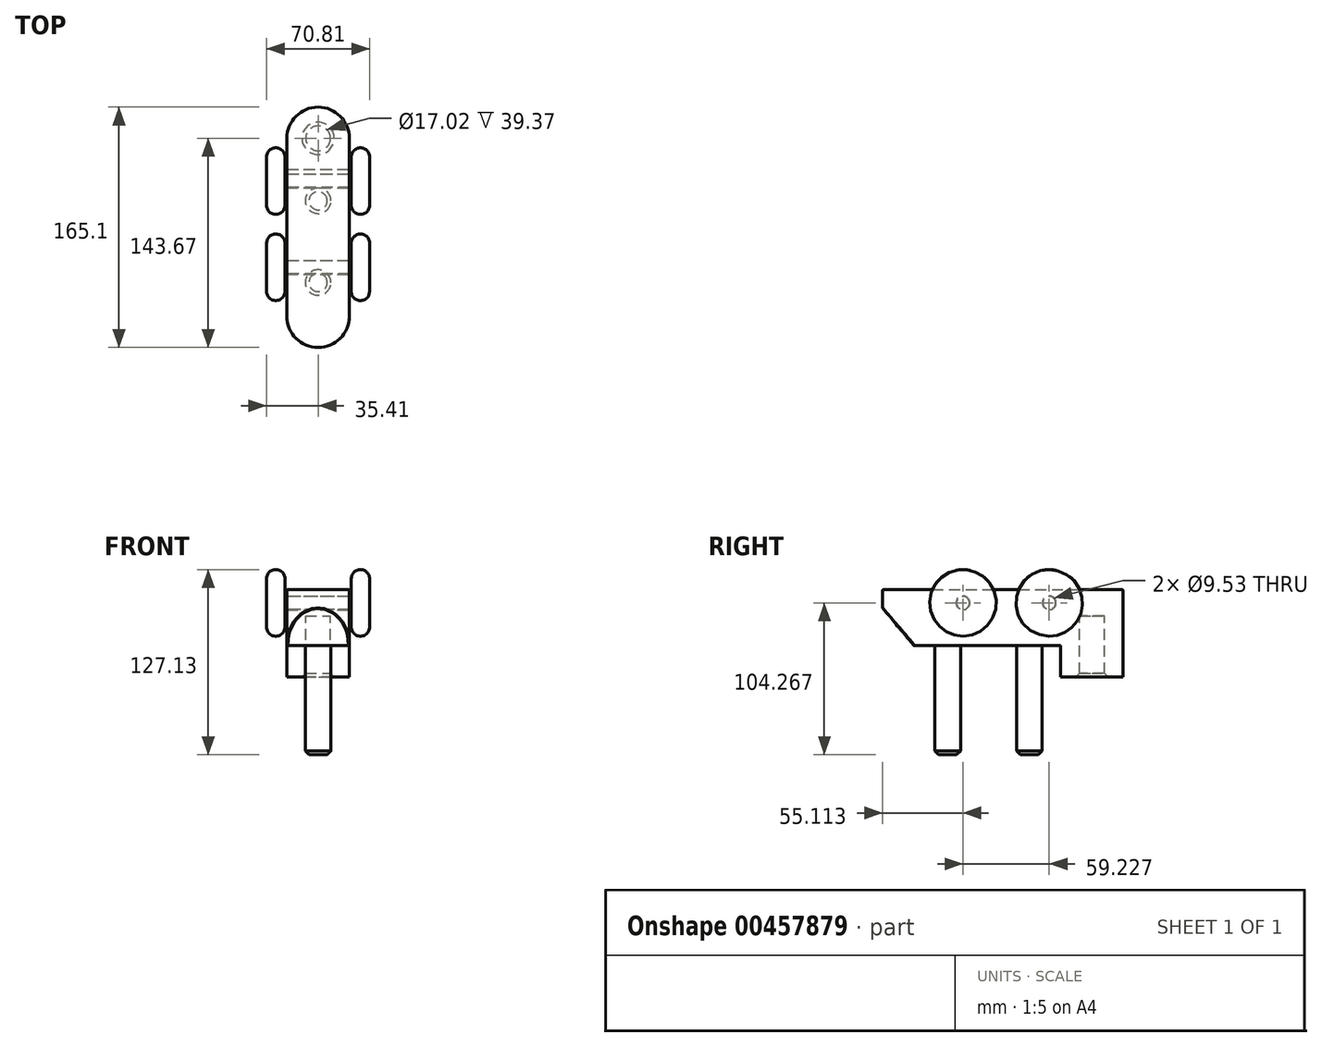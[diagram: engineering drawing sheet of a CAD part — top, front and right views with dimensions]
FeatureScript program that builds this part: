
annotation { "Feature Type Name" : "Feature", "Feature Type Description" : "" }
export const myFeature = defineFeature(function(context is Context, id is Id, definition is map)
    precondition{}
    {
        {
            var Q0;
            Q0=qCreatedBy(makeId("Top.planeOp"),FACE);
            var sketch = newSketch(context, id + "F0", { "sketchPlane" : qUnion([Q0])});
            skLineSegment(sketch, "E0", {"start": v(-21.43, 0) * mm, "end": v(-21.43, -122.24) * mm});
            skLineSegment(sketch, "E1", {"start": v(0, -143.67) * mm, "end": v(0, -143.67) * mm});
            skLineSegment(sketch, "E2", {"start": v(21.43, -122.24) * mm, "end": v(21.43, 0) * mm});
            skLineSegment(sketch, "E3", {"start": v(0, 21.43) * mm, "end": v(0, 21.43) * mm});
            skArc(sketch, "E4.filletArc", {"start": v(0, 21.43) * mm, "mid": v(-15.15, 15.15) * mm, "end": v(-21.43, 0) * mm});
            skArc(sketch, "E5.filletArc", {"start": v(21.43, 0) * mm, "mid": v(15.15, 15.15) * mm, "end": v(0, 21.43) * mm});
            skArc(sketch, "E6.filletArc", {"start": v(-21.43, -122.24) * mm, "mid": v(-15.15, -137.4) * mm, "end": v(0, -143.67) * mm});
            skArc(sketch, "E7.filletArc", {"start": v(0, -143.67) * mm, "mid": v(15.15, -137.4) * mm, "end": v(21.43, -122.24) * mm});
            skLineSegment(sketch, "E8", {"start": v(-21.43, -21.43) * mm, "end": v(21.43, -21.43) * mm});
            skCircle(sketch, "E9", {"center": v(0, 0) * mm, "radius": 8.5 * mm});
            skCircle(sketch, "E10", {"center": v(0, -99.03) * mm, "radius": 8.76 * mm});
            skCircle(sketch, "E11", {"center": v(0, -42.9) * mm, "radius": 8.76 * mm});
            skLineSegment(sketch, "E12", {"start": v(-21.43, -122.24) * mm, "end": v(21.43, -122.24) * mm, "construction": true});
            skSolve(sketch);
        }
        {
            var Q0;
            {var subQ3=sQuery(id+"F0.wireOp",EDGE,"E6.filletArc");Q0=makeQuery(id+"F0.imprint","IMPRINT",FACE,{"disambiguationData":[TD([[makeQuery(id+"F0.imprint","IMPRINT",EDGE,{"derivedFrom":subQ3}),1.0]])]});}
            var Q1;
            {var subQ0=sQuery(id+"F0.wireOp",EDGE,"E4.filletArc");Q1=makeQuery(id+"F0.imprint","IMPRINT",FACE,{"disambiguationData":[TD([[makeQuery(id+"F0.imprint","IMPRINT",EDGE,{"derivedFrom":subQ0}),1.0]])]});}
            var Q2;
            Q2=makeQuery(id+"F0.imprint","IMPRINT",FACE,{"disambiguationData":[TD([[makeQuery(id+"F0.imprint","IMPRINT",EDGE,{"derivedFrom":sQuery(id+"F0.wireOp",EDGE,"E11")}),1.0]])]});
            var Q3;
            Q3=makeQuery(id+"F0.imprint","IMPRINT",FACE,{"disambiguationData":[TD([[makeQuery(id+"F0.imprint","IMPRINT",EDGE,{"derivedFrom":sQuery(id+"F0.wireOp",EDGE,"E10")}),1.0]])]});
            var Q4;
            Q4=makeQuery(id+"F0.imprint","IMPRINT",FACE,{"disambiguationData":[TD([[makeQuery(id+"F0.imprint","IMPRINT",EDGE,{"derivedFrom":sQuery(id+"F0.wireOp",EDGE,"E9")}),1.0]])]});
            extrude(context, id + "F1", {"entities" : qUnion([Q0, Q1, Q2, Q3, Q4]), "depth" : 38.35 * mm, "offsetDistance" : 25.4 * mm});
        }
        {
            var Q0;
            {var subQ0=sQuery(id+"F0.wireOp",EDGE,"E4.filletArc");Q0=makeQuery(id+"F0.imprint","IMPRINT",FACE,{"disambiguationData":[TD([[makeQuery(id+"F0.imprint","IMPRINT",EDGE,{"derivedFrom":subQ0}),1.0]])]});}
            var Q1;
            Q1=makeQuery(id+"F0.imprint","IMPRINT",FACE,{"disambiguationData":[TD([[makeQuery(id+"F0.imprint","IMPRINT",EDGE,{"derivedFrom":sQuery(id+"F0.wireOp",EDGE,"E9")}),1.0]])]});
            extrude(context, id + "F2", {"entities" : qUnion([Q0, Q1]), "operationType" : NewBodyOperationType.REMOVE, "depth" : 20.32 * mm, "offsetDistance" : 25.4 * mm});
        }
        {
            var Q0;
            Q0=makeQuery(id+"F0.imprint","IMPRINT",FACE,{"disambiguationData":[TD([[makeQuery(id+"F0.imprint","IMPRINT",EDGE,{"derivedFrom":sQuery(id+"F0.wireOp",EDGE,"E11")}),1.0]])]});
            var Q1;
            Q1=makeQuery(id+"F0.imprint","IMPRINT",FACE,{"disambiguationData":[TD([[makeQuery(id+"F0.imprint","IMPRINT",EDGE,{"derivedFrom":sQuery(id+"F0.wireOp",EDGE,"E10")}),1.0]])]});
            extrude(context, id + "F3", {"entities" : qUnion([Q0, Q1]), "operationType" : NewBodyOperationType.ADD, "oppositeDirection" : true, "depth" : 74.93 * mm, "offsetDistance" : 25.4 * mm});
        }
        {
            var Q0;
            Q0=makeQuery(id+"F2.boolean.opBoolean","COPY",FACE,{"derivedFrom":makeQuery(id+"F2.opExtrude","CAP_FACE",FACE,{"disambiguationData":[OSD([sQuery(id+"F0.wireOp",EDGE,"E0"),sQuery(id+"F0.wireOp",EDGE,"E2"),sQuery(id+"F0.wireOp",EDGE,"E4.filletArc"),sQuery(id+"F0.wireOp",EDGE,"E5.filletArc"),sQuery(id+"F0.wireOp",EDGE,"E8")])],"isStart":false})});
            var sketch = newSketch(context, id + "F4", { "sketchPlane" : qUnion([Q0])});
            skCircle(sketch, "E13.0", {"center": v(0, 0) * mm, "radius": 8.5 * mm});
            skSolve(sketch);
        }
        {
            var Q0;
            Q0=makeQuery(id+"F4.imprint","IMPRINT",FACE,{"disambiguationData":[TD([[makeQuery(id+"F4.imprint","IMPRINT",EDGE,{"derivedFrom":sQuery(id+"F4.wireOp",EDGE,"E13.0")}),-1.0]])]});
            extrude(context, id + "F5", {"entities" : qUnion([Q0]), "operationType" : NewBodyOperationType.ADD, "depth" : 41.9 * mm, "offsetDistance" : 25.4 * mm});
        }
        {
            var Q0;
            Q0=makeQuery(id+"F5.opExtrude","CAP_EDGE",EDGE,{"disambiguationData":[OSD([sQuery(id+"F4.wireOp",EDGE,"E13.0")])],"isStart":false});
            var Q1;
            Q1=makeQuery(id+"F3.opExtrude","CAP_EDGE",EDGE,{"disambiguationData":[OSD([sQuery(id+"F0.wireOp",EDGE,"E11")])],"isStart":false});
            var Q2;
            Q2=makeQuery(id+"F3.opExtrude","CAP_EDGE",EDGE,{"disambiguationData":[OSD([sQuery(id+"F0.wireOp",EDGE,"E10")])],"isStart":false});
            chamfer(context, id + "F6", {"entities" : qUnion([Q0, Q1, Q2]), "width" : 2.54 * mm, "tangentPropagation" : true});
        }
        {
            var Q0;
            Q0=makeQuery(id+"F1.opExtrude","SWEPT_FACE",FACE,{"disambiguationData":[OSD([sQuery(id+"F0.wireOp",EDGE,"E2")])]});
            var sketch = newSketch(context, id + "F7", { "sketchPlane" : qUnion([Q0])});
            skLineSegment(sketch, "E14.0", {"start": v(-143.67, 0) * mm, "end": v(-122.24, 0) * mm});
            skLineSegment(sketch, "E15", {"start": v(-143.67, 0) * mm, "end": v(-143.67, 37.85) * mm});
            skLineSegment(sketch, "E16", {"start": v(-143.67, 25.72) * mm, "end": v(-122.24, 0) * mm});
            skLineSegment(sketch, "E17", {"start": v(0, 29.34) * mm, "end": v(-122.24, 29.34) * mm, "construction": true});
            skCircle(sketch, "E18", {"center": v(-29.33, 29.34) * mm, "radius": 4.45 * mm});
            skCircle(sketch, "E19", {"center": v(-88.56, 29.34) * mm, "radius": 4.45 * mm});
            skCircle(sketch, "E20", {"center": v(-29.33, 29.34) * mm, "radius": 4.76 * mm});
            skCircle(sketch, "E21", {"center": v(-88.56, 29.34) * mm, "radius": 4.76 * mm});
            skSolve(sketch);
        }
        {
            var Q0;
            Q0=makeQuery(id+"F7.imprint","IMPRINT",FACE,{"disambiguationData":[TD([[makeQuery(id+"F7.imprint","IMPRINT",EDGE,{"derivedFrom":sQuery(id+"F7.wireOp",EDGE,"E18")}),-1.0]])]});
            var Q1;
            Q1=makeQuery(id+"F7.imprint","IMPRINT",FACE,{"disambiguationData":[TD([[makeQuery(id+"F7.imprint","IMPRINT",EDGE,{"derivedFrom":sQuery(id+"F7.wireOp",EDGE,"E19")}),-1.0]])]});
            var Q2;
            Q2=makeQuery(id+"F7.imprint","IMPRINT",FACE,{"disambiguationData":[TD([[makeQuery(id+"F7.imprint","IMPRINT",EDGE,{"derivedFrom":sQuery(id+"F7.wireOp",EDGE,"E19")}),1.0]])]});
            var Q3;
            Q3=makeQuery(id+"F7.imprint","IMPRINT",FACE,{"disambiguationData":[TD([[makeQuery(id+"F7.imprint","IMPRINT",EDGE,{"derivedFrom":sQuery(id+"F7.wireOp",EDGE,"E18")}),1.0]])]});
            extrude(context, id + "F8", {"entities" : qUnion([Q0, Q1, Q2, Q3]), "operationType" : NewBodyOperationType.REMOVE, "endBound" : BoundingType.THROUGH_ALL, "oppositeDirection" : true, "depth" : 25.4 * mm, "offsetDistance" : 25.4 * mm});
        }
        {
            var Q0;
            Q0=makeQuery(id+"F7.imprint","IMPRINT",FACE,{"disambiguationData":[TD([[makeQuery(id+"F7.imprint","IMPRINT",EDGE,{"derivedFrom":sQuery(id+"F7.wireOp",EDGE,"E18")}),1.0]])]});
            var Q1;
            Q1=makeQuery(id+"F7.imprint","IMPRINT",FACE,{"disambiguationData":[TD([[makeQuery(id+"F7.imprint","IMPRINT",EDGE,{"derivedFrom":sQuery(id+"F7.wireOp",EDGE,"E19")}),1.0]])]});
            extrude(context, id + "F9", {"entities" : qUnion([Q0, Q1]), "depth" : 1.27 * mm, "offsetDistance" : 25.4 * mm});
        }
        {
            var Q0;
            Q0=makeQuery(id+"F9.opExtrude","CAP_FACE",FACE,{"disambiguationData":[OSD([sQuery(id+"F7.wireOp",EDGE,"E18")])],"isStart":false});
            var Q1;
            Q1=makeQuery(id+"F9.opExtrude","CAP_FACE",FACE,{"disambiguationData":[OSD([sQuery(id+"F7.wireOp",EDGE,"E19")])],"isStart":false});
            extrude(context, id + "F10", {"entities" : qUnion([Q0, Q1]), "operationType" : NewBodyOperationType.ADD, "oppositeDirection" : true, "depth" : 45.42 * mm, "offsetDistance" : 25.4 * mm});
        }
        {
            var Q0;
            Q0=makeQuery(id+"F9.opExtrude","CAP_FACE",FACE,{"disambiguationData":[OSD([sQuery(id+"F7.wireOp",EDGE,"E18")])],"isStart":false});
            var sketch = newSketch(context, id + "F11", { "sketchPlane" : qUnion([Q0])});
            skCircle(sketch, "E22", {"center": v(-29.33, 29.34) * mm, "radius": 22.86 * mm});
            skSolve(sketch);
        }
        {
            var Q0;
            Q0=makeQuery(id+"F9.opExtrude","CAP_FACE",FACE,{"disambiguationData":[OSD([sQuery(id+"F7.wireOp",EDGE,"E19")])],"isStart":false});
            var sketch = newSketch(context, id + "F12", { "sketchPlane" : qUnion([Q0])});
            skCircle(sketch, "E23", {"center": v(-88.56, 29.34) * mm, "radius": 22.86 * mm});
            skSolve(sketch);
        }
        {
            var Q0;
            Q0=makeQuery(id+"F10.opExtrude","CAP_FACE",FACE,{"disambiguationData":[OSD([sQuery(id+"F7.wireOp",EDGE,"E19")])],"isStart":false});
            var sketch = newSketch(context, id + "F13", { "sketchPlane" : qUnion([Q0])});
            skCircle(sketch, "E24", {"center": v(88.56, 29.34) * mm, "radius": 22.86 * mm});
            skSolve(sketch);
        }
        {
            var Q0;
            Q0=makeQuery(id+"F10.opExtrude","CAP_FACE",FACE,{"disambiguationData":[OSD([sQuery(id+"F7.wireOp",EDGE,"E18")])],"isStart":false});
            var sketch = newSketch(context, id + "F14", { "sketchPlane" : qUnion([Q0])});
            skCircle(sketch, "E25", {"center": v(29.33, 29.34) * mm, "radius": 22.86 * mm});
            skSolve(sketch);
        }
        {
            var Q0;
            Q0=makeQuery(id+"F11.imprint","IMPRINT",FACE,{"disambiguationData":[TD([[makeQuery(id+"F11.imprint","IMPRINT",EDGE,{"derivedFrom":sQuery(id+"F11.wireOp",EDGE,"E22")}),1.0]])]});
            var Q1;
            Q1=makeQuery(id+"F12.imprint","IMPRINT",FACE,{"disambiguationData":[TD([[makeQuery(id+"F12.imprint","IMPRINT",EDGE,{"derivedFrom":sQuery(id+"F12.wireOp",EDGE,"E23")}),1.0]])]});
            var Q2;
            Q2=makeQuery(id+"F11.imprint","IMPRINT",FACE,{"disambiguationData":[TD([[makeQuery(id+"F11.imprint","IMPRINT",EDGE,{"derivedFrom":makeQuery(id+"F9.opExtrude","CAP_EDGE",EDGE,{"disambiguationData":[OSD([sQuery(id+"F7.wireOp",EDGE,"E18")])],"isStart":false})}),1.0]])]});
            var Q3;
            Q3=makeQuery(id+"F12.imprint","IMPRINT",FACE,{"disambiguationData":[TD([[makeQuery(id+"F12.imprint","IMPRINT",EDGE,{"derivedFrom":makeQuery(id+"F9.opExtrude","CAP_EDGE",EDGE,{"disambiguationData":[OSD([sQuery(id+"F7.wireOp",EDGE,"E19")])],"isStart":false})}),1.0]])]});
            extrude(context, id + "F15", {"entities" : qUnion([Q0, Q1, Q2, Q3]), "depth" : 12.7 * mm, "offsetDistance" : 25.4 * mm});
        }
        {
            var Q0;
            Q0=makeQuery(id+"F13.imprint","IMPRINT",FACE,{"disambiguationData":[TD([[makeQuery(id+"F13.imprint","IMPRINT",EDGE,{"derivedFrom":sQuery(id+"F13.wireOp",EDGE,"E24")}),1.0]])]});
            var Q1;
            Q1=makeQuery(id+"F14.imprint","IMPRINT",FACE,{"disambiguationData":[TD([[makeQuery(id+"F14.imprint","IMPRINT",EDGE,{"derivedFrom":sQuery(id+"F14.wireOp",EDGE,"E25")}),1.0]])]});
            var Q2;
            Q2=makeQuery(id+"F14.imprint","IMPRINT",FACE,{"disambiguationData":[TD([[makeQuery(id+"F14.imprint","IMPRINT",EDGE,{"derivedFrom":makeQuery(id+"F10.opExtrude","CAP_EDGE",EDGE,{"disambiguationData":[OSD([sQuery(id+"F7.wireOp",EDGE,"E18")])],"isStart":false})}),-1.0]])]});
            var Q3;
            Q3=makeQuery(id+"F13.imprint","IMPRINT",FACE,{"disambiguationData":[TD([[makeQuery(id+"F13.imprint","IMPRINT",EDGE,{"derivedFrom":makeQuery(id+"F10.opExtrude","CAP_EDGE",EDGE,{"disambiguationData":[OSD([sQuery(id+"F7.wireOp",EDGE,"E19")])],"isStart":false})}),-1.0]])]});
            extrude(context, id + "F16", {"entities" : qUnion([Q0, Q1, Q2, Q3]), "depth" : 12.7 * mm, "offsetDistance" : 25.4 * mm});
        }
        {
            var Q0;
            Q0=makeQuery(id+"F16.opExtrude","CAP_FACE",FACE,{"disambiguationData":[OSD([sQuery(id+"F13.wireOp",EDGE,"E24")])],"isStart":false});
            var Q1;
            Q1=makeQuery(id+"F15.opExtrude","CAP_FACE",FACE,{"disambiguationData":[OSD([sQuery(id+"F12.wireOp",EDGE,"E23")])],"isStart":false});
            var Q2;
            Q2=makeQuery(id+"F15.opExtrude","CAP_FACE",FACE,{"disambiguationData":[OSD([sQuery(id+"F11.wireOp",EDGE,"E22")])],"isStart":false});
            var Q3;
            Q3=makeQuery(id+"F16.opExtrude","CAP_FACE",FACE,{"disambiguationData":[OSD([sQuery(id+"F14.wireOp",EDGE,"E25")])],"isStart":false});
            var Q4;
            Q4=makeQuery(id+"F16.opExtrude","CAP_FACE",FACE,{"disambiguationData":[OSD([sQuery(id+"F14.wireOp",EDGE,"E25")])],"isStart":true});
            var Q5;
            Q5=makeQuery(id+"F16.opExtrude","CAP_FACE",FACE,{"disambiguationData":[OSD([sQuery(id+"F13.wireOp",EDGE,"E24")])],"isStart":true});
            var Q6;
            Q6=makeQuery(id+"F15.opExtrude","CAP_FACE",FACE,{"disambiguationData":[OSD([sQuery(id+"F11.wireOp",EDGE,"E22")])],"isStart":true});
            var Q7;
            Q7=makeQuery(id+"F15.opExtrude","CAP_FACE",FACE,{"disambiguationData":[OSD([sQuery(id+"F12.wireOp",EDGE,"E23")])],"isStart":true});
            fillet(context, id + "F17", {"entities" : qUnion([Q0, Q1, Q2, Q3, Q4, Q5, Q6, Q7]), "radius" : 6.35 * mm, "tangentPropagation" : true, "allowEdgeOverflow" : false});
        }
        {
            var Q0;
            {var subQ0=sQuery(id+"F7.wireOp",EDGE,"E14.0");Q0=makeQuery(id+"F7.imprint","IMPRINT",FACE,{"disambiguationData":[TD([[makeQuery(id+"F7.imprint","IMPRINT",EDGE,{"derivedFrom":subQ0}),1.0]])]});}
            extrude(context, id + "F18", {"entities" : qUnion([Q0]), "operationType" : NewBodyOperationType.REMOVE, "endBound" : BoundingType.THROUGH_ALL, "oppositeDirection" : true, "depth" : 25.4 * mm, "offsetDistance" : 25.4 * mm});
        }
        {
            var Q0;
            Q0=makeQuery(id+"F2.boolean.opBoolean","COPY",EDGE,{"derivedFrom":makeQuery(id+"F2.opExtrude","CAP_EDGE",EDGE,{"disambiguationData":[OSD([sQuery(id+"F0.wireOp",EDGE,"E8")])],"isStart":true})});
            var Q1;
            Q1=makeQuery(id+"F1.opExtrude","CAP_FACE",FACE,{"disambiguationData":[OSD([sQuery(id+"F0.wireOp",EDGE,"E0"),sQuery(id+"F0.wireOp",EDGE,"E2"),sQuery(id+"F0.wireOp",EDGE,"E4.filletArc"),sQuery(id+"F0.wireOp",EDGE,"E5.filletArc"),sQuery(id+"F0.wireOp",EDGE,"E6.filletArc"),sQuery(id+"F0.wireOp",EDGE,"E7.filletArc")])],"isStart":true});
            var Q2;
            Q2=makeQuery(id+"F1.opExtrude","CAP_FACE",FACE,{"disambiguationData":[OSD([sQuery(id+"F0.wireOp",EDGE,"E0"),sQuery(id+"F0.wireOp",EDGE,"E2"),sQuery(id+"F0.wireOp",EDGE,"E4.filletArc"),sQuery(id+"F0.wireOp",EDGE,"E5.filletArc"),sQuery(id+"F0.wireOp",EDGE,"E6.filletArc"),sQuery(id+"F0.wireOp",EDGE,"E7.filletArc")])],"isStart":false});
            var Q3;
            Q3=makeQuery(id+"F2.boolean.opBoolean","COPY",EDGE,{"derivedFrom":makeQuery(id+"F2.opExtrude","SWEPT_EDGE",EDGE,{"disambiguationData":[OSD([sQuery(id+"F0.wireOp",EDGE,"E0"),sQuery(id+"F0.wireOp",EDGE,"E8")])]})});
            var Q4;
            Q4=makeQuery(id+"F2.boolean.opBoolean","COPY",EDGE,{"derivedFrom":makeQuery(id+"F2.opExtrude","CAP_EDGE",EDGE,{"disambiguationData":[OSD([sQuery(id+"F0.wireOp",EDGE,"E4.filletArc"),sQuery(id+"F0.wireOp",EDGE,"E5.filletArc")])],"isStart":false})});
            var Q5;
            Q5=makeQuery(id+"F2.boolean.opBoolean","COPY",EDGE,{"derivedFrom":makeQuery(id+"F2.opExtrude","CAP_EDGE",EDGE,{"disambiguationData":[OSD([sQuery(id+"F0.wireOp",EDGE,"E0")])],"isStart":false})});
            var Q6;
            Q6=makeQuery(id+"F2.boolean.opBoolean","COPY",EDGE,{"derivedFrom":makeQuery(id+"F2.opExtrude","SWEPT_EDGE",EDGE,{"disambiguationData":[OSD([sQuery(id+"F0.wireOp",EDGE,"E2"),sQuery(id+"F0.wireOp",EDGE,"E8")])]})});
            var Q7;
            Q7=makeQuery(id+"F5.opExtrude","CAP_EDGE",EDGE,{"disambiguationData":[OSD([sQuery(id+"F4.wireOp",EDGE,"E13.0")])],"isStart":true});
            fillet(context, id + "F19", {"entities" : qUnion([Q0, Q1, Q2, Q3, Q4, Q5, Q6, Q7]), "radius" : 0.5 * mm, "tangentPropagation" : true, "allowEdgeOverflow" : false});
        }
        {
            var Q0;
            Q0=makeQuery(id+"F18.boolean.opBoolean","INTERSECT",EDGE,{"derivedFrom":[makeQuery(id+"F1.opExtrude","SWEPT_FACE",FACE,{"disambiguationData":[OSD([sQuery(id+"F0.wireOp",EDGE,"E6.filletArc"),sQuery(id+"F0.wireOp",EDGE,"E7.filletArc")])]}),makeQuery(id+"F18.opExtrude","SWEPT_FACE",FACE,{"disambiguationData":[OSD([sQuery(id+"F7.wireOp",EDGE,"E16")])]})]});
            fillet(context, id + "F20", {"entities" : qUnion([Q0]), "radius" : 0.5 * mm, "tangentPropagation" : true, "allowEdgeOverflow" : false});
        }
    });
